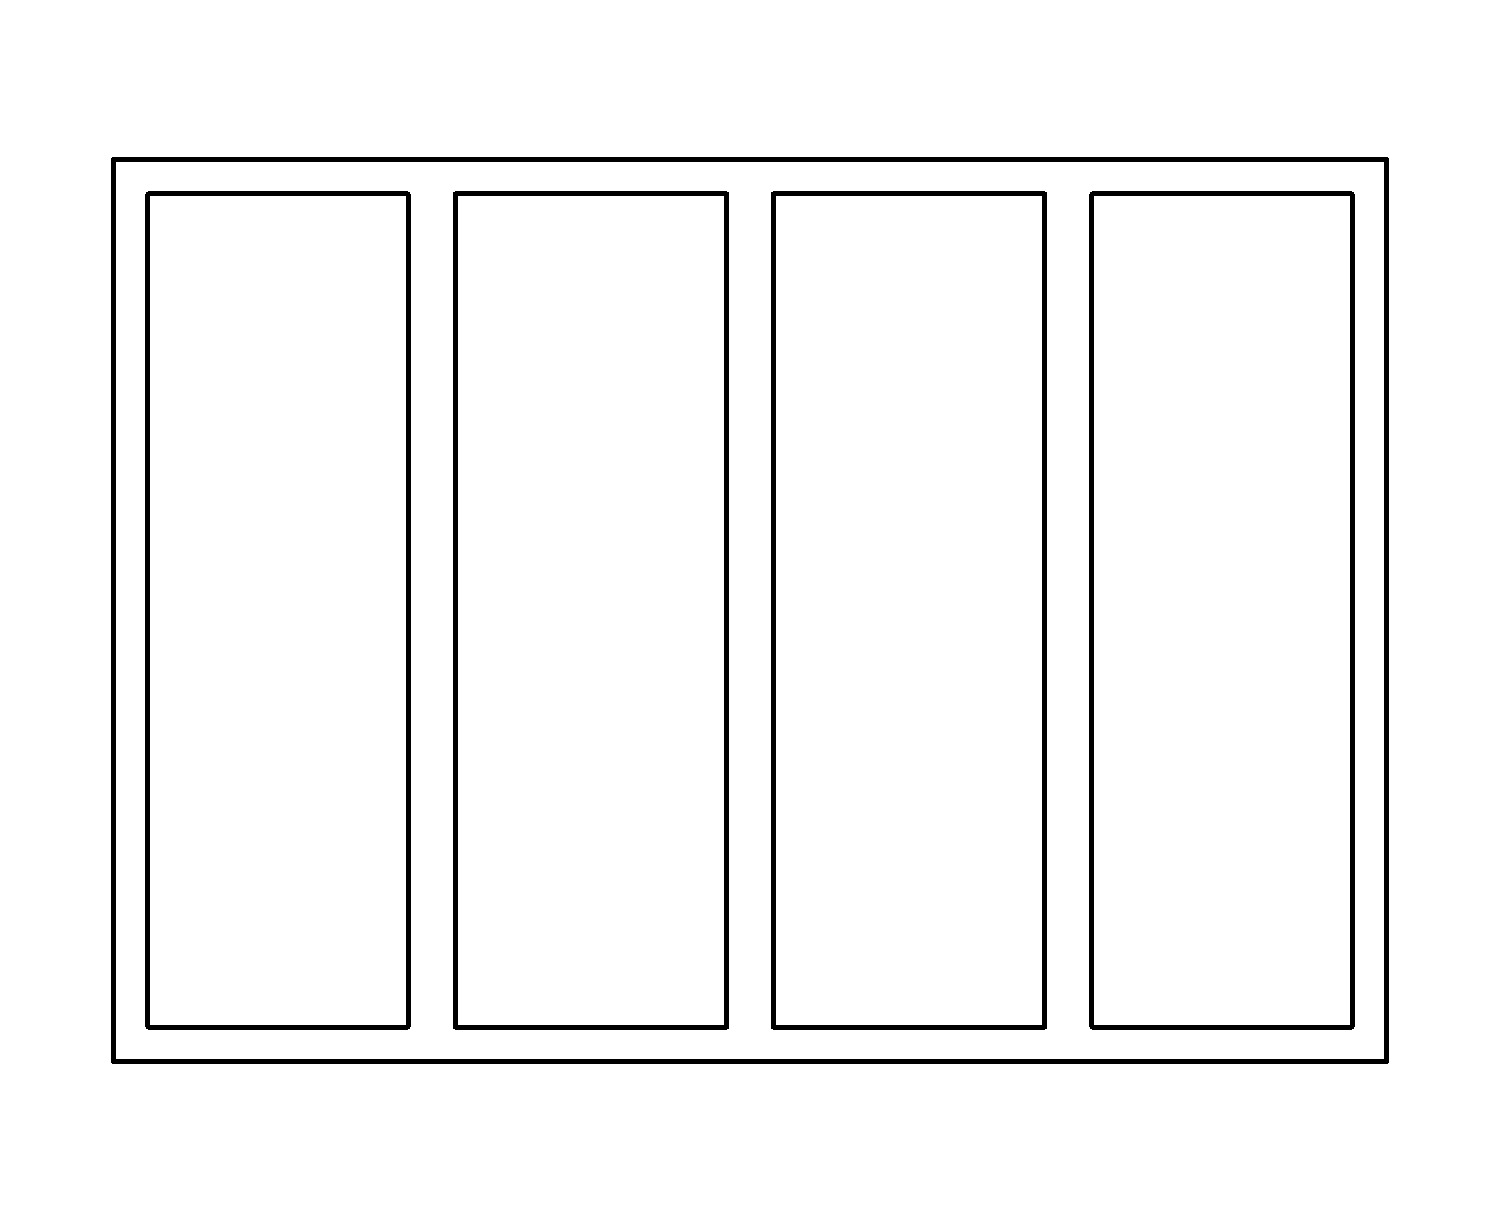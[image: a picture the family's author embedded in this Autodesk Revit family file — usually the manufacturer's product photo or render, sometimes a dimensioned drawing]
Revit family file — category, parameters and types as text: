
# Revit family: окна.rehau_четырехпольное
name_source: partatom
category: Окна
revit_build: Autodesk Revit 2017 (Build: 20171027_0315(x64)
units: mm (PartAtom-declared; Revit-internal decimal feet)

## family parameters
Всегда вертикально = Да
Заголовок OmniClass = Windows
Номер OmniClass = 23.30.20.00
Общий = Нет
Основа = Стена
При загрузке вырезать с полостями = Нет
Точка расчета площади = Нет

## types (2) — shared parameters
24_мм = 24мм 1-камерный
32_мм = 32мм 2-камерный
40_мм = 40мм 2-камерный
42_мм = 42мм 2-камерный
50_мм = 50мм 2-камерный
60_blitz_new = 60 BLITZ NEW
60_euro_64 = 60 EURO (коробка 64, импост 78, створка 60)
60_euro_68 = 60 EURO (коробка 68, импост 78, створка 60)
60_euro_76 = 60 EURO (коробка 76, импост 86, створка 74)
70_delight_78 = 70 DELIGHT
70_grazio_55 = 70 GRAZIO (коробка 55)
70_grazio_63 = 70 GRAZIO (коробка 63)
80_intelio_58r = 80 INTELIO (коробка 58, створка R57)
80_intelio_58z = 80 INTELIO (коробка 58, створка Z57)
80_intelio_65r = 80 INTELIO (коробка 65, створка R57)
80_intelio_65z = 80 INTELIO (коробка 65, створка Z57)
ADSK_Обозначение = ГОСТ 30674-99
URL = https://www.rehau.com
sp_energy = Энергосберегающие стекла
sp_gaz = Заполненный газом
sp_standart = Обычный стеклопакет
sp_triplex = Триплекс
Аналитическая конструкция = Окна с одинарным остеклением - для жилых зданий
Высота подоконника по умолчанию = 900 мм
Группа модели = ОП
Длина профилей коробки = 7040 мм
Замыкание стены = По основе
Заполнение стеклопакета = Обычный стеклопакет
Изготовитель = Rehau
Изображение типоразмера = схема_четырехпольное.png
Коэффициент теплопередачи (U) = 5.7361 Вт/(м²·K)
Коэффициент теплопритока от солнечного излучения = 0.86
Материал коробки = <По категории>
Материал отлива = <По категории>
Материал подоконника = <По категории>
Материал стекла = <По категории>
Описание = проем.окно
Примерная высота = 1460 мм
Примерная ширина = 2060 мм
Пропускание видимого света = 0.9
Равные створки = Да
Створка слева = 400 мм
Створка справа = 400 мм
Створка центральная левая = 400 мм
Створка центральная правая = 860 мм
Термостойкость = 0.1743 (м²·K)/Вт
Тип створки центр слева = створка : глухая
Тип створки центр справа = створка : глухая
глухая_створка = створка : глухая
обозначение_проема_высота = 243 мм
обозначение_проема_ширина = 343 мм
створка_слева_размер = 515 мм
створка_справа_размер = 515 мм
створка_центр_слева_размер = 515 мм
таблица выбора = каталог профилей Rehau

## per-type parameters (varying)
| type | Тип створки слева | Тип створки справа |
| 2060х1460 (створка и глухое) | створка : левая-откидная | створка : правая-откидная |
| 2060х1460 (глухое) | створка : глухая | створка : глухая |
